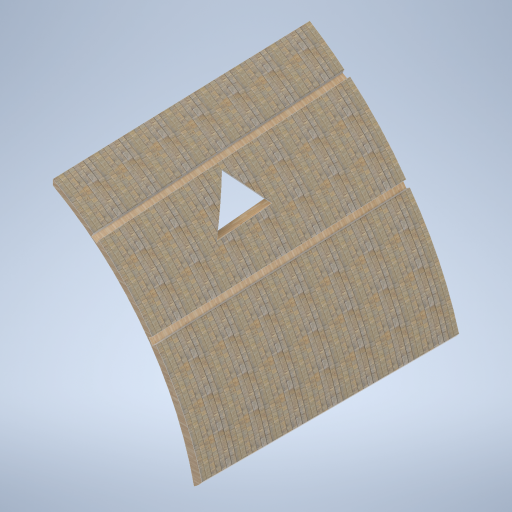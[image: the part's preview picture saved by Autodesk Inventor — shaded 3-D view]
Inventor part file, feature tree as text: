
AUTODESK INVENTOR PART (.ipt)
format: ipt  version: 2024.2 (Build 282272000, 272)  size: 528,896 bytes
history: native  units: mm
features: sketch x3, plane x3, loft x1, extrude x1
ambient origin geometry x8: Origin, YZ Plane, XZ Plane, XY Plane, X Axis, Y Axis, Z Axis, Center Point
bodies: Solid1 (feature_tree)
feature tree (8):
  sketch  "Sketch1"  dims[d5=0.0mm d6=-8101.0mm d7=800.0mm]
  plane  "Work Plane2"
  loft  "Loft1"
  plane  "Work Plane3"
  extrude  "Extrusion1"  TaperAngle=0.0deg  [1 undecoded]
  plane  "Work Plane1"
  sketch  "Sketch2"  dims[d8=0.0mm d9=90.0deg d10=0.0mm d11=90.0deg]
  sketch  "Sketch3"  dims[d12=2600.0mm d13=0.0mm d14=0.0mm d15=500.0mm d16=0.872665mm]
note: 1 required parameter value undecoded (feature->parameter linkage not recoverable at this tier; creation-order binding heuristic only, values carry confidence <= 0.55)
